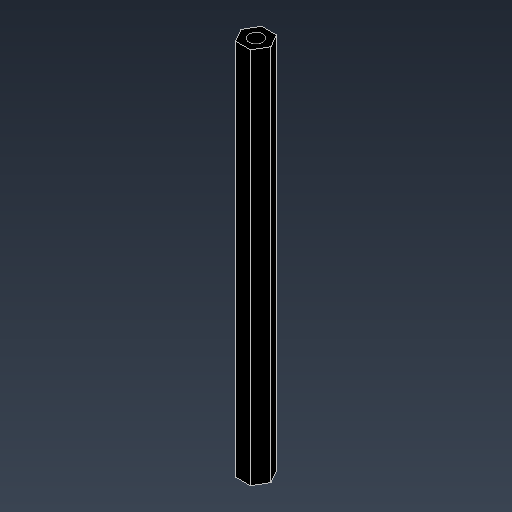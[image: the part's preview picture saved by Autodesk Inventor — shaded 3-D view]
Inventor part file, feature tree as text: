
AUTODESK INVENTOR PART (.ipt)
format: ipt  version: 2025 (Build 290162010, 162A)  size: 99,328 bytes
history: native  units: mm
features: extrude x1, sketch x1
ambient origin geometry x8: Origin, YZ Plane, XZ Plane, XY Plane, X Axis, Y Axis, Z Axis, Center Point
bodies: Solid1 (feature_tree)
feature tree (2):
  extrude  "Extrusion1"  Depth=80.0mm
  sketch  "Sketch1"  dims[d0=5.5mm d1=3.0mm d2=80.0mm d3=0.0mm d4=0.5mm d5=0.872665mm]
